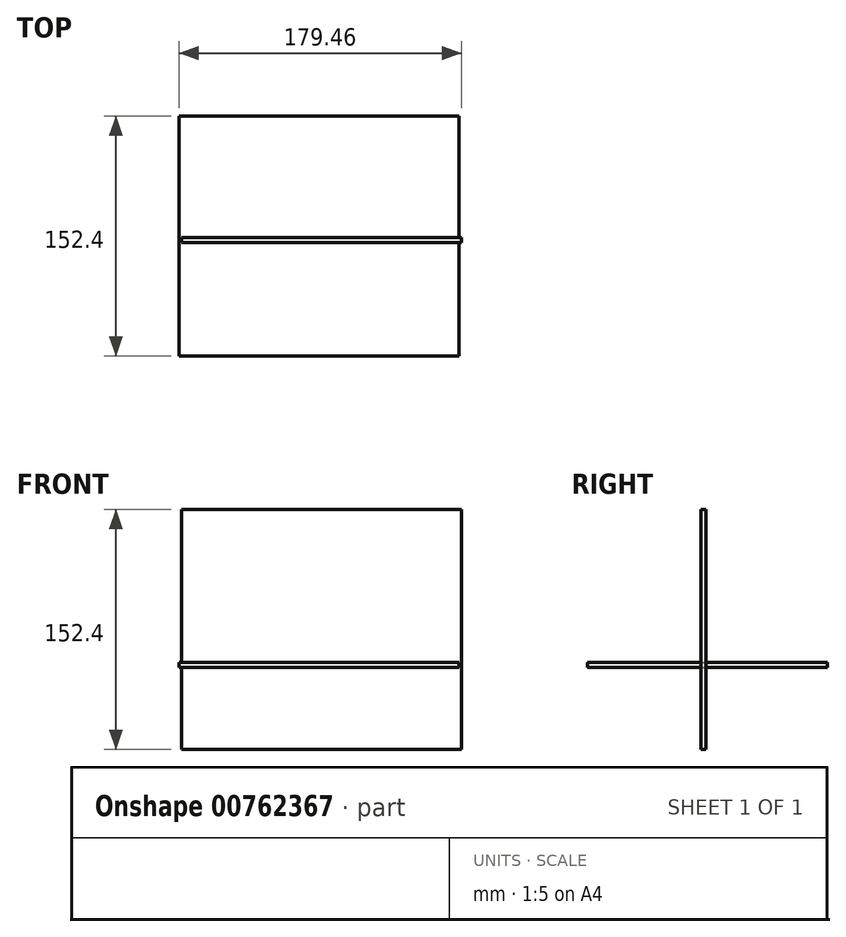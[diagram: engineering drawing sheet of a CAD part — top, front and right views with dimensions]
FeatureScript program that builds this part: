
annotation { "Feature Type Name" : "Feature", "Feature Type Description" : "" }
export const myFeature = defineFeature(function(context is Context, id is Id, definition is map)
    precondition{}
    {
        {
            var Q0;
            Q0=qCreatedBy(makeId("Top.planeOp"),FACE);
            var sketch = newSketch(context, id + "F0", { "sketchPlane" : qUnion([Q0])});
            skLineSegment(sketch, "E0.bottom", {"start": v(-90.02, 77.21) * mm, "end": v(87.78, 77.21) * mm});
            skLineSegment(sketch, "E0.top", {"start": v(-90.02, -75.19) * mm, "end": v(87.78, -75.19) * mm});
            skLineSegment(sketch, "E0.left", {"start": v(-90.02, 77.21) * mm, "end": v(-90.02, -75.19) * mm});
            skLineSegment(sketch, "E0.right", {"start": v(87.78, 77.21) * mm, "end": v(87.78, -75.19) * mm});
            skSolve(sketch);
        }
        {
            var Q0;
            Q0=makeQuery(id+"F0.imprint","IMPRINT",FACE,{"disambiguationData":[TD([[makeQuery(id+"F0.imprint","IMPRINT",EDGE,{"derivedFrom":sQuery(id+"F0.wireOp",EDGE,"E0.bottom")}),-1.0]])]});
            extrude(context, id + "F1", {"entities" : qUnion([Q0]), "depth" : 3.17 * mm, "offsetDistance" : 25.4 * mm});
        }
        {
            var Q0;
            Q0=qCreatedBy(makeId("Front.planeOp"),FACE);
            var sketch = newSketch(context, id + "F2", { "sketchPlane" : qUnion([Q0])});
            skLineSegment(sketch, "E1.bottom", {"start": v(-88.36, 100.46) * mm, "end": v(89.44, 100.46) * mm});
            skLineSegment(sketch, "E1.top", {"start": v(-88.36, -51.94) * mm, "end": v(89.44, -51.94) * mm});
            skLineSegment(sketch, "E1.left", {"start": v(-88.36, 100.46) * mm, "end": v(-88.36, -51.94) * mm});
            skLineSegment(sketch, "E1.right", {"start": v(89.44, 100.46) * mm, "end": v(89.44, -51.94) * mm});
            skSolve(sketch);
        }
        {
            var Q0;
            Q0=makeQuery(id+"F2.imprint","IMPRINT",FACE,{"disambiguationData":[TD([[makeQuery(id+"F2.imprint","IMPRINT",EDGE,{"derivedFrom":sQuery(id+"F2.wireOp",EDGE,"E1.bottom")}),-1.0]])]});
            extrude(context, id + "F3", {"entities" : qUnion([Q0]), "operationType" : NewBodyOperationType.ADD, "depth" : 3.17 * mm, "offsetDistance" : 25.4 * mm});
        }
    });
